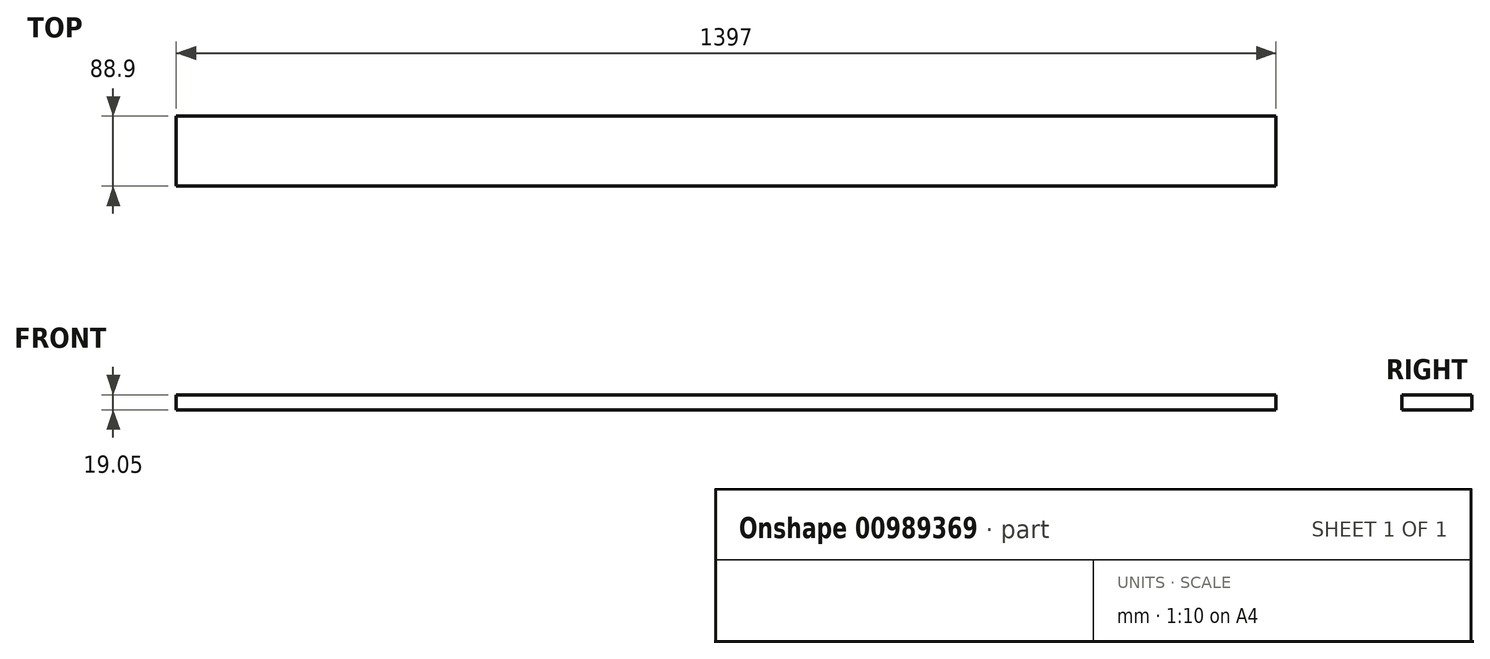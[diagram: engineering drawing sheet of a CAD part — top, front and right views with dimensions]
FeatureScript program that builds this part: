
annotation { "Feature Type Name" : "Feature", "Feature Type Description" : "" }
export const myFeature = defineFeature(function(context is Context, id is Id, definition is map)
    precondition{}
    {
        {
            var Q0;
            Q0=qCreatedBy(makeId("Right.planeOp"),FACE);
            var sketch = newSketch(context, id + "F0", { "sketchPlane" : qUnion([Q0])});
            skLineSegment(sketch, "E0.bottom", {"start": v(-63.5, 13.63) * mm, "end": v(25.4, 13.63) * mm});
            skLineSegment(sketch, "E0.top", {"start": v(-63.5, -5.42) * mm, "end": v(25.4, -5.42) * mm});
            skLineSegment(sketch, "E0.left", {"start": v(-63.5, 13.63) * mm, "end": v(-63.5, -5.42) * mm});
            skLineSegment(sketch, "E0.right", {"start": v(25.4, 13.63) * mm, "end": v(25.4, -5.42) * mm});
            skSolve(sketch);
        }
        {
            var Q0;
            Q0=makeQuery(id+"F0.imprint","IMPRINT",FACE,{"disambiguationData":[TD([[makeQuery(id+"F0.imprint","IMPRINT",EDGE,{"derivedFrom":sQuery(id+"F0.wireOp",EDGE,"E0.bottom")}),-1.0]])]});
            extrude(context, id + "F1", {"entities" : qUnion([Q0]), "depth" : 1397 * mm, "offsetDistance" : 25.4 * mm});
        }
    });
